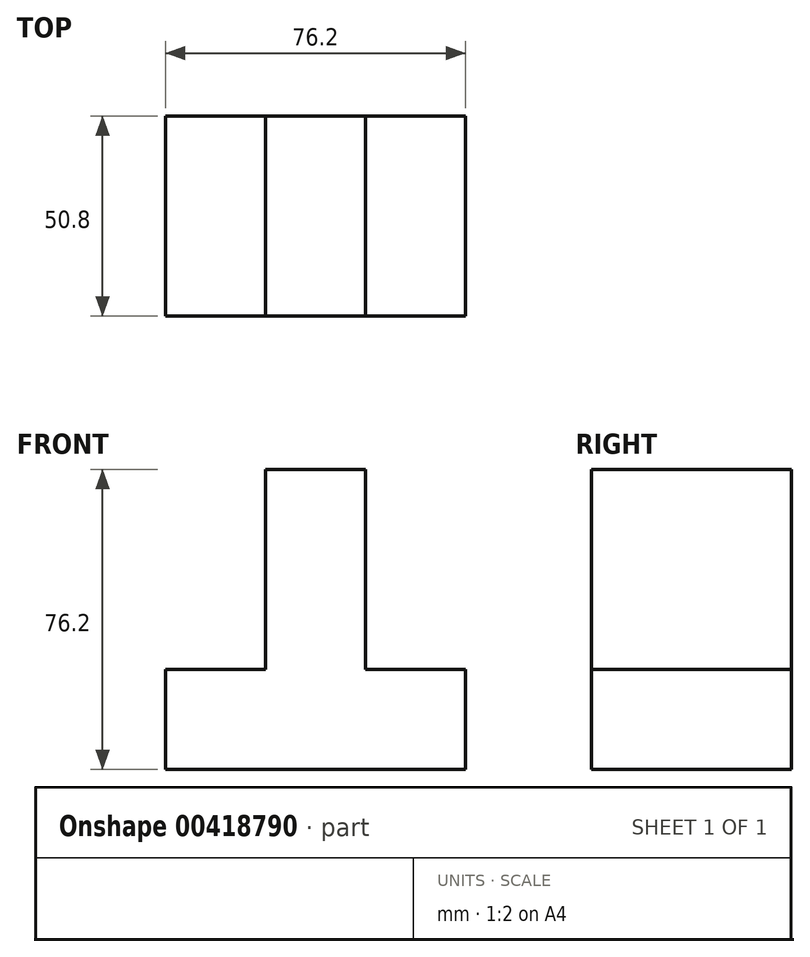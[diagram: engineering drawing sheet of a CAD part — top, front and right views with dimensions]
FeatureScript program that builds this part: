
annotation { "Feature Type Name" : "Feature", "Feature Type Description" : "" }
export const myFeature = defineFeature(function(context is Context, id is Id, definition is map)
    precondition{}
    {
        {
            var Q0;
            Q0=qCreatedBy(makeId("Front.planeOp"),FACE);
            var sketch = newSketch(context, id + "F0", { "sketchPlane" : qUnion([Q0])});
            skLineSegment(sketch, "E0", {"start": v(0, 0) * mm, "end": v(76.2, 0) * mm});
            skLineSegment(sketch, "E1", {"start": v(76.2, 0) * mm, "end": v(76.2, 25.4) * mm});
            skLineSegment(sketch, "E2", {"start": v(76.2, 25.4) * mm, "end": v(50.8, 25.4) * mm});
            skLineSegment(sketch, "E3", {"start": v(50.8, 25.4) * mm, "end": v(50.8, 76.2) * mm});
            skLineSegment(sketch, "E4", {"start": v(50.8, 76.2) * mm, "end": v(25.4, 76.2) * mm});
            skLineSegment(sketch, "E5", {"start": v(25.4, 76.2) * mm, "end": v(25.4, 25.4) * mm});
            skLineSegment(sketch, "E6", {"start": v(25.4, 25.4) * mm, "end": v(0, 25.4) * mm});
            skLineSegment(sketch, "E7", {"start": v(0, 25.4) * mm, "end": v(0, 0) * mm});
            skSolve(sketch);
        }
        {
            var Q0;
            Q0=makeQuery(id+"F0.imprint","IMPRINT",FACE,{"disambiguationData":[TD([[makeQuery(id+"F0.imprint","IMPRINT",EDGE,{"derivedFrom":sQuery(id+"F0.wireOp",EDGE,"E0")}),1.0]])]});
            extrude(context, id + "F1", {"entities" : qUnion([Q0]), "depth" : 50.8 * mm});
        }
    });
